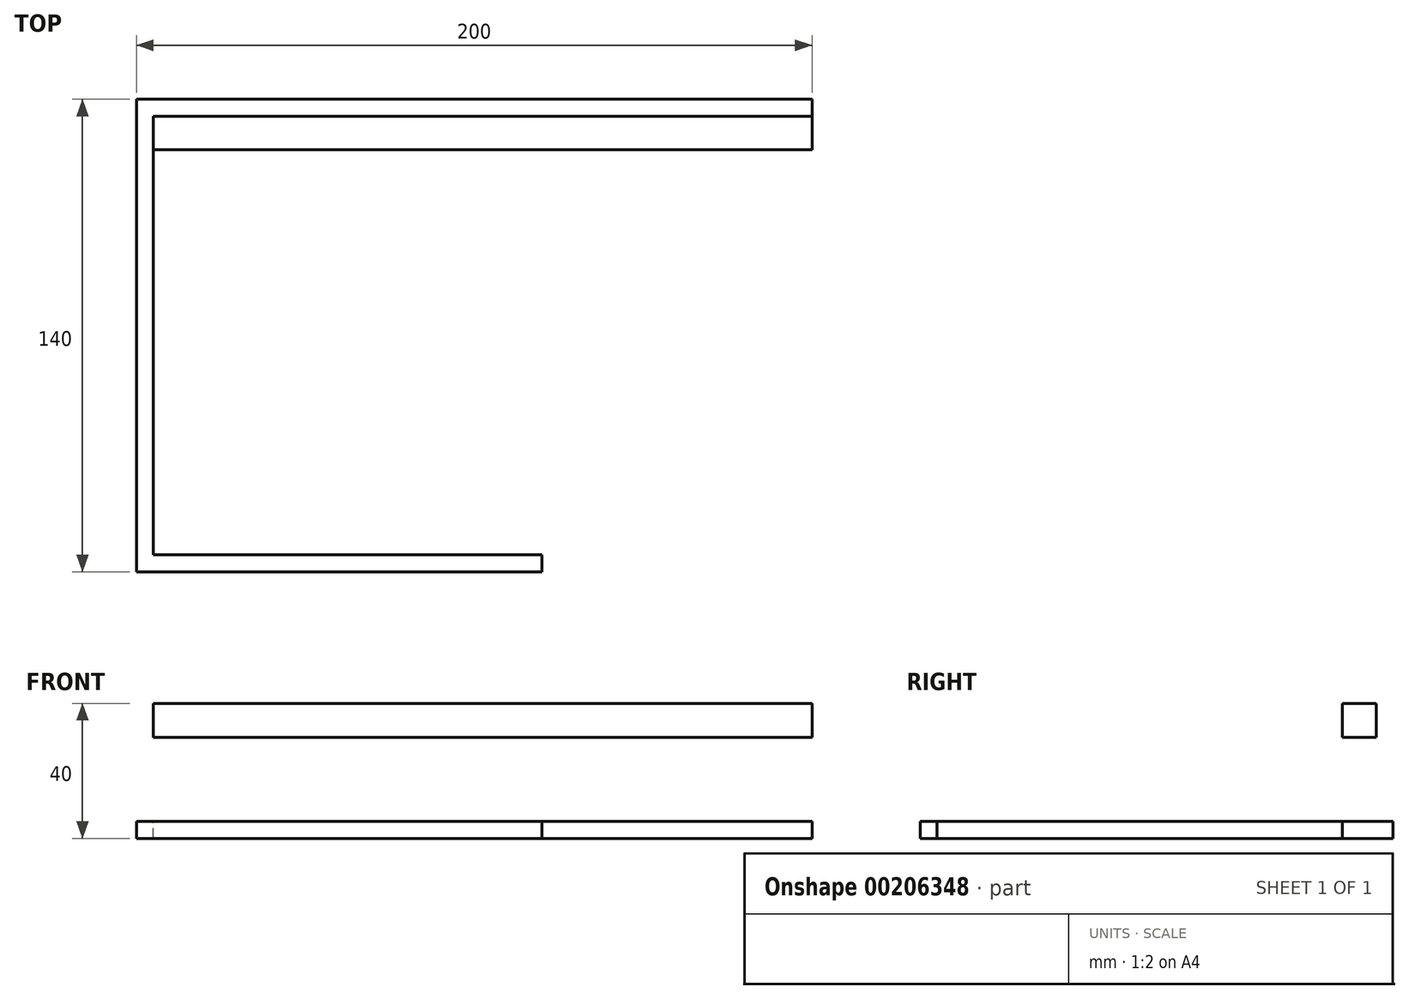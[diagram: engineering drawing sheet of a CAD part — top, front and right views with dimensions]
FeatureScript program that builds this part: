
annotation { "Feature Type Name" : "Feature", "Feature Type Description" : "" }
export const myFeature = defineFeature(function(context is Context, id is Id, definition is map)
    precondition{}
    {
        {
            var Q0;
            Q0=qCreatedBy(makeId("Top.planeOp"),FACE);
            var sketch = newSketch(context, id + "F0", { "sketchPlane" : qUnion([Q0])});
            skLineSegment(sketch, "E0.bottom", {"start": v(0, 0) * mm, "end": v(-120, 0) * mm});
            skLineSegment(sketch, "E0.top", {"start": v(0, -140) * mm, "end": v(-120, -140) * mm});
            skLineSegment(sketch, "E0.left", {"start": v(0, 0) * mm, "end": v(0, -140) * mm});
            skLineSegment(sketch, "E0.right", {"start": v(-120, 0) * mm, "end": v(-120, -140) * mm});
            skLineSegment(sketch, "E1.bottom", {"start": v(-120, 0) * mm, "end": v(-115, 0) * mm});
            skLineSegment(sketch, "E1.top", {"start": v(-120, -140) * mm, "end": v(-115, -140) * mm});
            skLineSegment(sketch, "E1.right", {"start": v(-115, -5) * mm, "end": v(-115, -135) * mm});
            skLineSegment(sketch, "E2.bottom", {"start": v(0, 0) * mm, "end": v(-115, 0) * mm});
            skLineSegment(sketch, "E2.top", {"start": v(0, -5) * mm, "end": v(-115, -5) * mm});
            skLineSegment(sketch, "E2.left", {"start": v(0, 0) * mm, "end": v(0, -5) * mm});
            skLineSegment(sketch, "E3.bottom", {"start": v(0, -140) * mm, "end": v(-115, -140) * mm});
            skLineSegment(sketch, "E3.top", {"start": v(0, -135) * mm, "end": v(-115, -135) * mm});
            skLineSegment(sketch, "E3.left", {"start": v(0, -140) * mm, "end": v(0, -135) * mm});
            skLineSegment(sketch, "E4.top", {"start": v(0, -15) * mm, "end": v(-115, -15) * mm});
            skLineSegment(sketch, "E4.left", {"start": v(0, -5) * mm, "end": v(0, -15) * mm});
            skLineSegment(sketch, "E4.right", {"start": v(-115, -5) * mm, "end": v(-115, -15) * mm});
            skSolve(sketch);
        }
        {
            var Q0;
            Q0=makeQuery(id+"F0.imprint","IMPRINT",FACE,{"disambiguationData":[TD([[makeQuery(id+"F0.imprint","IMPRINT",EDGE,{"derivedFrom":sQuery(id+"F0.wireOp",EDGE,"E0.left")}),-1.0]])]});
            var Q1;
            Q1=makeQuery(id+"F0.imprint","IMPRINT",FACE,{"disambiguationData":[TD([[makeQuery(id+"F0.imprint","IMPRINT",EDGE,{"derivedFrom":sQuery(id+"F0.wireOp",EDGE,"E1.bottom")}),-1.0]])]});
            var Q2;
            Q2=makeQuery(id+"F0.imprint","IMPRINT",FACE,{"disambiguationData":[TD([[makeQuery(id+"F0.imprint","IMPRINT",EDGE,{"derivedFrom":sQuery(id+"F0.wireOp",EDGE,"E2.top")}),1.0]])]});
            extrude(context, id + "F1", {"entities" : qUnion([Q0, Q1, Q2]), "oppositeDirection" : true, "depth" : 5 * mm});
        }
        {
            var Q0;
            Q0=makeQuery(id+"F0.imprint","IMPRINT",FACE,{"disambiguationData":[TD([[makeQuery(id+"F0.imprint","IMPRINT",EDGE,{"derivedFrom":sQuery(id+"F0.wireOp",EDGE,"E2.top")}),1.0]])]});
            var Q1;
            Q1=makeQuery(id+"F0.imprint","IMPRINT",FACE,{"disambiguationData":[TD([[makeQuery(id+"F0.imprint","IMPRINT",EDGE,{"derivedFrom":sQuery(id+"F0.wireOp",EDGE,"E1.bottom")}),-1.0]])]});
            extrude(context, id + "F2", {"entities" : qUnion([Q0, Q1]), "operationType" : NewBodyOperationType.ADD, "depth" : 35 * mm});
        }
        {
            var Q0;
            Q0=makeQuery(id+"F0.imprint","IMPRINT",FACE,{"disambiguationData":[TD([[makeQuery(id+"F0.imprint","IMPRINT",EDGE,{"derivedFrom":sQuery(id+"F0.wireOp",EDGE,"E2.top")}),1.0]])]});
            extrude(context, id + "F3", {"entities" : qUnion([Q0]), "operationType" : NewBodyOperationType.REMOVE, "depth" : 25 * mm});
        }
        {
            var Q0;
            {var subQ0=sQuery(id+"F0.wireOp",EDGE,"E3.left");var subQ1=sQuery(id+"F0.wireOp",EDGE,"E4.left");var subQ2=sQuery(id+"F0.wireOp",EDGE,"E2.left");Q0=makeQuery(id+"F2.boolean.opBoolean","MERGE",FACE,{"derivedFrom":[makeQuery(id+"F1.opExtrude","SWEPT_FACE",FACE,{"disambiguationData":[OSD([sQuery(id+"F0.wireOp",EDGE,"E0.left"),subQ2,subQ0,subQ1])]}),makeQuery(id+"F2.opExtrude","SWEPT_FACE",FACE,{"disambiguationData":[OSD([subQ2,subQ1])]}),makeQuery(id+"F2.opExtrude","SWEPT_FACE",FACE,{"disambiguationData":[OSD([subQ0])]})]});}
            extrude(context, id + "F4", {"entities" : qUnion([Q0]), "operationType" : NewBodyOperationType.ADD, "depth" : 80 * mm, "offsetDistance" : 25 * mm});
        }
    });
